FCSTD DOCUMENT  (FreeCAD 0.20R26155 (Git))
Label: snescart
License: All rights reserved
LicenseURL: http://en.wikipedia.org/wiki/All_rights_reserved
objects: Sketcher::SketchObject×5, PartDesign::Body×1
note: 6 computed .brp shape members not serialized (recipe doc carries the construction recipe); baked Part::Feature solids carry a one-line shape summary decoded from their .brp

FEATURE [Sketcher::SketchObject] Sketch  label="Edge_Cuts_0.15"
  FullyConstrained = true
  MapMode = 5
  Support = -> [XY_Plane]
  sketch-geometry (17):
    g0: LineSegment StartX=102 StartY=0 StartZ=0 EndX=102 EndY=17.5 EndZ=0
    g1: LineSegment StartX=102 StartY=17.5 StartZ=0 EndX=100.5 EndY=17.5 EndZ=0
    g2: LineSegment StartX=100.5 StartY=17.5 StartZ=0 EndX=100.5 EndY=23.5 EndZ=0
    g3: LineSegment StartX=100.5 StartY=23.5 StartZ=0 EndX=98 EndY=23.5 EndZ=0
    g4: LineSegment StartX=98 StartY=23.5 StartZ=0 EndX=98 EndY=25 EndZ=0
    g5: LineSegment StartX=98 StartY=25 StartZ=0 EndX=102 EndY=25 EndZ=0
    g6: LineSegment StartX=102 StartY=25 StartZ=0 EndX=102 EndY=48 EndZ=0
    g7: LineSegment StartX=98 StartY=52 StartZ=0 EndX=4 EndY=52 EndZ=0
    g8: LineSegment StartX=4e-14 StartY=48 StartZ=0 EndX=4e-14 EndY=16.4 EndZ=0
    g9: LineSegment StartX=4e-14 StartY=16.4 StartZ=0 EndX=4 EndY=16.4 EndZ=0
    g10: LineSegment StartX=4 StartY=16.4 StartZ=0 EndX=4 EndY=14.9 EndZ=0
    g11: LineSegment StartX=4 StartY=14.9 StartZ=0 EndX=1.5 EndY=14.9 EndZ=0
    g12: LineSegment StartX=1.5 StartY=14.9 StartZ=0 EndX=1.5 EndY=8.9 EndZ=0
    g13: LineSegment StartX=1.5 StartY=8.9 StartZ=0 EndX=0 EndY=8.9 EndZ=0
    g14: LineSegment StartX=0 StartY=8.9 StartZ=0 EndX=0 EndY=0 EndZ=0
    g15: ArcOfCircle CenterX=4 CenterY=48 CenterZ=0 NormalX=0 NormalY=0 NormalZ=1 AngleXU=0 Radius=4 StartAngle=1.5708 EndAngle=3.14159
    g16: ArcOfCircle CenterX=98 CenterY=48 CenterZ=0 NormalX=0 NormalY=0 NormalZ=1 AngleXU=0 Radius=4 StartAngle=1.84e-14 EndAngle=1.5708
  constraints (49):
    c: Vertical(g0)
    c: Coincident(g0,g1)
    c: Horizontal(g1)
    c: Coincident(g1,g2)
    c: Vertical(g2)
    c: Coincident(g2,g3)
    c: Horizontal(g3)
    c: Coincident(g3,g4)
    c: Vertical(g4)
    c: Coincident(g4,g5)
    c: Horizontal(g5)
    c: Coincident(g5,g6)
    c: Horizontal(g7)
    c: Vertical(g8)
    c: Coincident(g8,g9)
    c: Coincident(g9,g10)
    c: Vertical(g10)
    c: Coincident(g10,g11)
    c: Horizontal(g11)
    c: Coincident(g11,g12)
    c: Vertical(g12)
    c: Coincident(g12,g13)
    c: Horizontal(g13)
    c: Coincident(g13,g14)
    c: Vertical(g14)
    c: Horizontal(g9)
    c: Vertical(g6)
    c: DistanceX(g5,g5) = 4
    c: DistanceX(g2,g5) = 1.5
    c: DistanceX(g9,g9) = 4
    c: DistanceX(g11,g11) = 2.5
    c: DistanceX(g13,g13) = 1.5
    c: DistanceY(g10,g10) = 1.5
    c: DistanceY(g12,g12) = 6
    c: DistanceY(g14,g14) = 8.9
    c: DistanceY(g0,g5) = 25
    c: DistanceY(g4,g4) = 1.5
    c: DistanceY(g2,g2) = 6
    c: Coincident(g14,g-1)
    c: PointOnObject(g0,g-1)
    c: DistanceX(g14,g0) = 102
    c: Tangent(g7,g15) = -1.5708
    c: Tangent(g8,g15) = -1.5708
    c: Tangent(g6,g16) = -1.5708
    c: Tangent(g7,g16) = -1.5708
    c: Equal(g15,g16)
    c: DistanceX(g8,g6) = 102
    c: DistanceY(g14,g8) = 48
    c: Radius(g15) = 4
FEATURE [Sketcher::SketchObject] Sketch001  label="Edge_Cuts_0.016"
  FullyConstrained = true
  MapMode = 5
  Support = -> [XY_Plane]
  sketch-geometry (5):
    g0: LineSegment StartX=0 StartY=0 StartZ=0 EndX=21 EndY=0 EndZ=0
    g1: LineSegment StartX=21 StartY=0 StartZ=0 EndX=21 EndY=-10 EndZ=0
    g2: LineSegment StartX=21 StartY=-10 StartZ=0 EndX=81 EndY=-10 EndZ=0
    g3: LineSegment StartX=81 StartY=-10 StartZ=0 EndX=81 EndY=0 EndZ=0
    g4: LineSegment StartX=81 StartY=0 StartZ=0 EndX=102 EndY=0 EndZ=0
  constraints (15):
    c: Coincident(g-1,g0)
    c: PointOnObject(g0,g-1)
    c: Coincident(g0,g1)
    c: Vertical(g1)
    c: Coincident(g1,g2)
    c: Horizontal(g2)
    c: Coincident(g2,g3)
    c: PointOnObject(g3,g-1)
    c: Vertical(g3)
    c: Coincident(g3,g4)
    c: PointOnObject(g4,g-1)
    c: DistanceX(g0,g4) = 102
    c: Equal(g0,g4)
    c: DistanceX(g0,g0) = 21
    c: DistanceY(g3,g3) = 10
FEATURE [Sketcher::SketchObject] Sketch002  label="F_Pads_TH_SMD"
  ExternalGeometry = -> [Sketch001]
  FullyConstrained = true
  MapMode = 5
  Support = -> [XY_Plane]
  sketch-geometry (92):
    g0: LineSegment StartX=22.25 StartY=-3 StartZ=0 EndX=24.25 EndY=-3 EndZ=0
    g1: LineSegment StartX=24.25 StartY=-3 StartZ=0 EndX=24.25 EndY=-10 EndZ=0
    g2: LineSegment StartX=24.25 StartY=-10 StartZ=0 EndX=22.25 EndY=-10 EndZ=0
    g3: LineSegment StartX=22.25 StartY=-10 StartZ=0 EndX=22.25 EndY=-3 EndZ=0
    g4: LineSegment StartX=25.25 StartY=-3 StartZ=0 EndX=26.75 EndY=-3 EndZ=0
    g5: LineSegment StartX=26.75 StartY=-3 StartZ=0 EndX=26.75 EndY=-10 EndZ=0
    g6: LineSegment StartX=26.75 StartY=-10 StartZ=0 EndX=25.25 EndY=-10 EndZ=0
    g7: LineSegment StartX=25.25 StartY=-10 StartZ=0 EndX=25.25 EndY=-3 EndZ=0
    g8: LineSegment StartX=27.75 StartY=-3 StartZ=0 EndX=29.25 EndY=-3 EndZ=0
    g9: LineSegment StartX=29.25 StartY=-3 StartZ=0 EndX=29.25 EndY=-10 EndZ=0
    g10: LineSegment StartX=29.25 StartY=-10 StartZ=0 EndX=27.75 EndY=-10 EndZ=0
    g11: LineSegment StartX=27.75 StartY=-10 StartZ=0 EndX=27.75 EndY=-3 EndZ=0
    g12: LineSegment StartX=30.25 StartY=-10 StartZ=0 EndX=31.75 EndY=-10 EndZ=0
    g13: LineSegment StartX=31.75 StartY=-10 StartZ=0 EndX=31.75 EndY=-3 EndZ=0
    g14: LineSegment StartX=31.75 StartY=-3 StartZ=0 EndX=30.25 EndY=-3 EndZ=0
    g15: LineSegment StartX=30.25 StartY=-3 StartZ=0 EndX=30.25 EndY=-10 EndZ=0
    g16: LineSegment StartX=32.75 StartY=-10 StartZ=0 EndX=34.25 EndY=-10 EndZ=0
    g17: LineSegment StartX=34.25 StartY=-10 StartZ=0 EndX=34.25 EndY=-3 EndZ=0
    g18: LineSegment StartX=34.25 StartY=-3 StartZ=0 EndX=32.75 EndY=-3 EndZ=0
    g19: LineSegment StartX=32.75 StartY=-3 StartZ=0 EndX=32.75 EndY=-10 EndZ=0
    g20: LineSegment StartX=35.25 StartY=-10 StartZ=0 EndX=36.75 EndY=-10 EndZ=0
    g21: LineSegment StartX=36.75 StartY=-10 StartZ=0 EndX=36.75 EndY=-3 EndZ=0
    g22: LineSegment StartX=36.75 StartY=-3 StartZ=0 EndX=35.25 EndY=-3 EndZ=0
    g23: LineSegment StartX=35.25 StartY=-3 StartZ=0 EndX=35.25 EndY=-10 EndZ=0
    g24: LineSegment StartX=37.75 StartY=-10 StartZ=0 EndX=39.25 EndY=-10 EndZ=0
    g25: LineSegment StartX=39.25 StartY=-10 StartZ=0 EndX=39.25 EndY=-3 EndZ=0
    g26: LineSegment StartX=39.25 StartY=-3 StartZ=0 EndX=37.75 EndY=-3 EndZ=0
    g27: LineSegment StartX=37.75 StartY=-3 StartZ=0 EndX=37.75 EndY=-10 EndZ=0
    g28: LineSegment StartX=40.25 StartY=-10 StartZ=0 EndX=41.75 EndY=-10 EndZ=0
    g29: LineSegment StartX=41.75 StartY=-10 StartZ=0 EndX=41.75 EndY=-3 EndZ=0
    g30: LineSegment StartX=41.75 StartY=-3 StartZ=0 EndX=40.25 EndY=-3 EndZ=0
    g31: LineSegment StartX=40.25 StartY=-3 StartZ=0 EndX=40.25 EndY=-10 EndZ=0
    g32: LineSegment StartX=42.75 StartY=-10 StartZ=0 EndX=44.25 EndY=-10 EndZ=0
    g33: LineSegment StartX=44.25 StartY=-10 StartZ=0 EndX=44.25 EndY=-3 EndZ=0
    g34: LineSegment StartX=44.25 StartY=-3 StartZ=0 EndX=42.75 EndY=-3 EndZ=0
    g35: LineSegment StartX=42.75 StartY=-3 StartZ=0 EndX=42.75 EndY=-10 EndZ=0
    g36: LineSegment StartX=45.25 StartY=-10 StartZ=0 EndX=46.75 EndY=-10 EndZ=0
    g37: LineSegment StartX=46.75 StartY=-10 StartZ=0 EndX=46.75 EndY=-3 EndZ=0
    g38: LineSegment StartX=46.75 StartY=-3 StartZ=0 EndX=45.25 EndY=-3 EndZ=0
    g39: LineSegment StartX=45.25 StartY=-3 StartZ=0 EndX=45.25 EndY=-10 EndZ=0
    g40: LineSegment StartX=47.75 StartY=-10 StartZ=0 EndX=49.25 EndY=-10 EndZ=0
    g41: LineSegment StartX=49.25 StartY=-10 StartZ=0 EndX=49.25 EndY=-3 EndZ=0
    g42: LineSegment StartX=49.25 StartY=-3 StartZ=0 EndX=47.75 EndY=-3 EndZ=0
    g43: LineSegment StartX=47.75 StartY=-3 StartZ=0 EndX=47.75 EndY=-10 EndZ=0
    g44: LineSegment StartX=50.25 StartY=-10 StartZ=0 EndX=51.75 EndY=-10 EndZ=0
    g45: LineSegment StartX=51.75 StartY=-10 StartZ=0 EndX=51.75 EndY=-3 EndZ=0
    g46: LineSegment StartX=51.75 StartY=-3 StartZ=0 EndX=50.25 EndY=-3 EndZ=0
    g47: LineSegment StartX=50.25 StartY=-3 StartZ=0 EndX=50.25 EndY=-10 EndZ=0
    g48: LineSegment StartX=52.75 StartY=-10 StartZ=0 EndX=54.25 EndY=-10 EndZ=0
    g49: LineSegment StartX=54.25 StartY=-10 StartZ=0 EndX=54.25 EndY=-3 EndZ=0
    g50: LineSegment StartX=54.25 StartY=-3 StartZ=0 EndX=52.75 EndY=-3 EndZ=0
    g51: LineSegment StartX=52.75 StartY=-3 StartZ=0 EndX=52.75 EndY=-10 EndZ=0
    g52: LineSegment StartX=55.25 StartY=-10 StartZ=0 EndX=56.75 EndY=-10 EndZ=0
    g53: LineSegment StartX=56.75 StartY=-10 StartZ=0 EndX=56.75 EndY=-3 EndZ=0
    g54: LineSegment StartX=56.75 StartY=-3 StartZ=0 EndX=55.25 EndY=-3 EndZ=0
    g55: LineSegment StartX=55.25 StartY=-3 StartZ=0 EndX=55.25 EndY=-10 EndZ=0
    g56: LineSegment StartX=57.75 StartY=-10 StartZ=0 EndX=59.25 EndY=-10 EndZ=0
    g57: LineSegment StartX=59.25 StartY=-10 StartZ=0 EndX=59.25 EndY=-3 EndZ=0
    g58: LineSegment StartX=59.25 StartY=-3 StartZ=0 EndX=57.75 EndY=-3 EndZ=0
    g59: LineSegment StartX=57.75 StartY=-3 StartZ=0 EndX=57.75 EndY=-10 EndZ=0
    g60: LineSegment StartX=60.25 StartY=-10 StartZ=0 EndX=61.75 EndY=-10 EndZ=0
    g61: LineSegment StartX=61.75 StartY=-10 StartZ=0 EndX=61.75 EndY=-3 EndZ=0
    g62: LineSegment StartX=61.75 StartY=-3 StartZ=0 EndX=60.25 EndY=-3 EndZ=0
    g63: LineSegment StartX=60.25 StartY=-3 StartZ=0 EndX=60.25 EndY=-10 EndZ=0
    g64: LineSegment StartX=62.75 StartY=-10 StartZ=0 EndX=64.25 EndY=-10 EndZ=0
    g65: LineSegment StartX=64.25 StartY=-10 StartZ=0 EndX=64.25 EndY=-3 EndZ=0
    g66: LineSegment StartX=64.25 StartY=-3 StartZ=0 EndX=62.75 EndY=-3 EndZ=0
    g67: LineSegment StartX=62.75 StartY=-3 StartZ=0 EndX=62.75 EndY=-10 EndZ=0
    g68: LineSegment StartX=65.25 StartY=-10 StartZ=0 EndX=66.75 EndY=-10 EndZ=0
    g69: LineSegment StartX=66.75 StartY=-10 StartZ=0 EndX=66.75 EndY=-3 EndZ=0
    g70: LineSegment StartX=66.75 StartY=-3 StartZ=0 EndX=65.25 EndY=-3 EndZ=0
    g71: LineSegment StartX=65.25 StartY=-3 StartZ=0 EndX=65.25 EndY=-10 EndZ=0
    g72: LineSegment StartX=67.75 StartY=-10 StartZ=0 EndX=69.25 EndY=-10 EndZ=0
    g73: LineSegment StartX=69.25 StartY=-10 StartZ=0 EndX=69.25 EndY=-3 EndZ=0
    g74: LineSegment StartX=69.25 StartY=-3 StartZ=0 EndX=67.75 EndY=-3 EndZ=0
    g75: LineSegment StartX=67.75 StartY=-3 StartZ=0 EndX=67.75 EndY=-10 EndZ=0
    g76: LineSegment StartX=70.25 StartY=-10 StartZ=0 EndX=71.75 EndY=-10 EndZ=0
    g77: LineSegment StartX=71.75 StartY=-10 StartZ=0 EndX=71.75 EndY=-3 EndZ=0
    g78: LineSegment StartX=71.75 StartY=-3 StartZ=0 EndX=70.25 EndY=-3 EndZ=0
    g79: LineSegment StartX=70.25 StartY=-3 StartZ=0 EndX=70.25 EndY=-10 EndZ=0
    g80: LineSegment StartX=72.75 StartY=-10 StartZ=0 EndX=74.25 EndY=-10 EndZ=0
    g81: LineSegment StartX=74.25 StartY=-10 StartZ=0 EndX=74.25 EndY=-3 EndZ=0
    g82: LineSegment StartX=74.25 StartY=-3 StartZ=0 EndX=72.75 EndY=-3 EndZ=0
    g83: LineSegment StartX=72.75 StartY=-3 StartZ=0 EndX=72.75 EndY=-10 EndZ=0
    g84: LineSegment StartX=75.25 StartY=-10 StartZ=0 EndX=76.75 EndY=-10 EndZ=0
    g85: LineSegment StartX=76.75 StartY=-10 StartZ=0 EndX=76.75 EndY=-3 EndZ=0
    g86: LineSegment StartX=76.75 StartY=-3 StartZ=0 EndX=75.25 EndY=-3 EndZ=0
    g87: LineSegment StartX=75.25 StartY=-3 StartZ=0 EndX=75.25 EndY=-10 EndZ=0
    g88: LineSegment StartX=77.75 StartY=-10 StartZ=0 EndX=79.75 EndY=-10 EndZ=0
    g89: LineSegment StartX=79.75 StartY=-10 StartZ=0 EndX=79.75 EndY=-3 EndZ=0
    g90: LineSegment StartX=79.75 StartY=-3 StartZ=0 EndX=77.75 EndY=-3 EndZ=0
    g91: LineSegment StartX=77.75 StartY=-3 StartZ=0 EndX=77.75 EndY=-10 EndZ=0
  constraints (276):
    c: Coincident(g0,g1)
    c: Coincident(g1,g2)
    c: Coincident(g2,g3)
    c: Coincident(g3,g0)
    c: Horizontal(g0)
    c: Horizontal(g2)
    c: Vertical(g1)
    c: Vertical(g3)
    c: Coincident(g4,g5)
    c: Coincident(g5,g6)
    c: Coincident(g6,g7)
    c: Coincident(g7,g4)
    c: Horizontal(g4)
    c: Horizontal(g6)
    c: Vertical(g5)
    c: Vertical(g7)
    c: DistanceY(g3,g3) = 7
    c: PointOnObject(g1,g-4)
    c: PointOnObject(g6,g-4)
    c: DistanceX(g2,g2) = 2
    c: DistanceX(g6,g6) = 1.5
    c: Equal(g3,g7)
    c: DistanceX(g-4,g2) = 1.25
    c: DistanceX(g0,g4) = 1
    c: Coincident(g8,g9)
    c: Coincident(g9,g10)
    c: Coincident(g10,g11)
    c: Coincident(g11,g8)
    c: Horizontal(g8)
    c: Horizontal(g10)
    c: Vertical(g9)
    c: Vertical(g11)
    c: PointOnObject(g9,g-4)
    c: Coincident(g12,g13)
    c: Coincident(g13,g14)
    c: Coincident(g14,g15)
    c: Coincident(g15,g12)
    c: Horizontal(g12)
    c: Horizontal(g14)
    c: Vertical(g13)
    c: Vertical(g15)
    c: PointOnObject(g12,g-4)
    c: Coincident(g16,g17)
    c: Coincident(g17,g18)
    c: Coincident(g18,g19)
    c: Coincident(g19,g16)
    c: Horizontal(g16)
    c: Horizontal(g18)
    c: Vertical(g17)
    c: Vertical(g19)
    c: PointOnObject(g16,g-4)
    c: Coincident(g20,g21)
    c: Coincident(g21,g22)
    c: Coincident(g22,g23)
    c: Coincident(g23,g20)
    c: Horizontal(g20)
    c: Horizontal(g22)
    c: Vertical(g21)
    c: Vertical(g23)
    c: PointOnObject(g20,g-4)
    c: Coincident(g24,g25)
    c: Coincident(g25,g26)
    c: Coincident(g26,g27)
    c: Coincident(g27,g24)
    c: Horizontal(g24)
    c: Horizontal(g26)
    c: Vertical(g25)
    c: Vertical(g27)
    c: PointOnObject(g24,g-4)
    c: Coincident(g28,g29)
    c: Coincident(g29,g30)
    c: Coincident(g30,g31)
    c: Coincident(g31,g28)
    c: Horizontal(g28)
    c: Horizontal(g30)
    c: Vertical(g29)
    c: Vertical(g31)
    c: PointOnObject(g28,g-4)
    c: Coincident(g32,g33)
    c: Coincident(g33,g34)
    c: Coincident(g34,g35)
    c: Coincident(g35,g32)
    c: Horizontal(g32)
    c: Horizontal(g34)
    c: Vertical(g33)
    c: Vertical(g35)
    c: PointOnObject(g32,g-4)
    c: Coincident(g36,g37)
    c: Coincident(g37,g38)
    c: Coincident(g38,g39)
    c: Coincident(g39,g36)
    c: Horizontal(g36)
    c: Horizontal(g38)
    c: Vertical(g37)
    c: Vertical(g39)
    c: PointOnObject(g36,g-4)
    c: Coincident(g40,g41)
    c: Coincident(g41,g42)
    c: Coincident(g42,g43)
    c: Coincident(g43,g40)
    c: Horizontal(g40)
    c: Horizontal(g42)
    c: Vertical(g41)
    c: Vertical(g43)
    c: PointOnObject(g40,g-4)
    c: Coincident(g44,g45)
    c: Coincident(g45,g46)
    c: Coincident(g46,g47)
    c: Coincident(g47,g44)
    c: Horizontal(g44)
    c: Horizontal(g46)
    c: Vertical(g45)
    c: Vertical(g47)
    c: PointOnObject(g44,g-4)
    c: Coincident(g48,g49)
    c: Coincident(g49,g50)
    c: Coincident(g50,g51)
    c: Coincident(g51,g48)
    c: Horizontal(g48)
    c: Horizontal(g50)
    c: Vertical(g49)
    c: Vertical(g51)
    c: PointOnObject(g48,g-4)
    c: Coincident(g52,g53)
    c: Coincident(g53,g54)
    c: Coincident(g54,g55)
    c: Coincident(g55,g52)
    c: Horizontal(g52)
    c: Horizontal(g54)
    c: Vertical(g53)
    c: Vertical(g55)
    c: PointOnObject(g52,g-4)
    c: Coincident(g56,g57)
    c: Coincident(g57,g58)
    c: Coincident(g58,g59)
    c: Coincident(g59,g56)
    c: Horizontal(g56)
    c: Horizontal(g58)
    c: Vertical(g57)
    c: Vertical(g59)
    c: PointOnObject(g56,g-4)
    c: Coincident(g60,g61)
    c: Coincident(g61,g62)
    c: Coincident(g62,g63)
    c: Coincident(g63,g60)
    c: Horizontal(g60)
    c: Horizontal(g62)
    c: Vertical(g61)
    c: Vertical(g63)
    c: PointOnObject(g60,g-4)
    c: Coincident(g64,g65)
    c: Coincident(g65,g66)
    c: Coincident(g66,g67)
    c: Coincident(g67,g64)
    c: Horizontal(g64)
    c: Horizontal(g66)
    c: Vertical(g65)
    c: Vertical(g67)
    c: PointOnObject(g64,g-4)
    c: Coincident(g68,g69)
    c: Coincident(g69,g70)
    c: Coincident(g70,g71)
    c: Coincident(g71,g68)
    c: Horizontal(g68)
    c: Horizontal(g70)
    c: Vertical(g69)
    c: Vertical(g71)
    c: PointOnObject(g68,g-4)
    c: Coincident(g72,g73)
    c: Coincident(g73,g74)
    c: Coincident(g74,g75)
    c: Coincident(g75,g72)
    c: Horizontal(g72)
    c: Horizontal(g74)
    c: Vertical(g73)
    c: Vertical(g75)
    c: PointOnObject(g72,g-4)
    c: Coincident(g76,g77)
    c: Coincident(g77,g78)
    c: Coincident(g78,g79)
    c: Coincident(g79,g76)
    c: Horizontal(g76)
    c: Horizontal(g78)
    c: Vertical(g77)
    c: Vertical(g79)
    c: PointOnObject(g76,g-4)
    c: Equal(g11,g15)
    c: Equal(g15,g19)
    c: Equal(g19,g23)
    c: Equal(g23,g27)
    c: Equal(g27,g31)
    c: Equal(g31,g35)
    c: Equal(g35,g39)
    c: Equal(g39,g43)
    c: Equal(g43,g47)
    c: Equal(g47,g51)
    c: Equal(g51,g55)
    c: Equal(g55,g59)
    c: Equal(g59,g63)
    c: Equal(g63,g67)
    c: Equal(g67,g71)
    c: Equal(g71,g75)
    c: Equal(g75,g79)
    c: Equal(g79,g7)
    c: Equal(g54,g58)
    c: Equal(g58,g62)
    c: Equal(g62,g66)
    c: Equal(g66,g70)
    c: Equal(g70,g74)
    c: Equal(g74,g78)
    c: Equal(g78,g50)
    c: Equal(g50,g46)
    c: Equal(g46,g42)
    c: Equal(g42,g38)
    c: Equal(g38,g34)
    c: Equal(g34,g30)
    c: Equal(g30,g26)
    c: Equal(g26,g22)
    c: Equal(g22,g18)
    c: Equal(g18,g14)
    c: Equal(g14,g8)
    c: Equal(g8,g4)
    c: DistanceX(g5,g10) = 1
    c: DistanceX(g9,g12) = 1
    c: DistanceX(g12,g16) = 1
    c: DistanceX(g16,g20) = 1
    c: DistanceX(g20,g24) = 1
    c: DistanceX(g24,g28) = 1
    c: DistanceX(g28,g32) = 1
    c: DistanceX(g32,g36) = 1
    c: DistanceX(g36,g40) = 1
    c: DistanceX(g40,g44) = 1
    c: DistanceX(g44,g48) = 1
    c: DistanceX(g48,g52) = 1
    c: DistanceX(g52,g56) = 1
    c: DistanceX(g56,g60) = 1
    c: DistanceX(g60,g64) = 1
    c: DistanceX(g64,g68) = 1
    c: DistanceX(g68,g72) = 1
    c: DistanceX(g72,g76) = 1
    c: Coincident(g80,g81)
    c: Coincident(g81,g82)
    c: Coincident(g82,g83)
    c: Coincident(g83,g80)
    c: Horizontal(g80)
    c: Horizontal(g82)
    c: Vertical(g81)
    c: Vertical(g83)
    c: PointOnObject(g80,g-4)
    c: Coincident(g84,g85)
    c: Coincident(g85,g86)
    c: Coincident(g86,g87)
    c: Coincident(g87,g84)
    c: Horizontal(g84)
    c: Horizontal(g86)
    c: Vertical(g85)
    c: Vertical(g87)
    c: PointOnObject(g84,g-4)
    c: Coincident(g88,g89)
    c: Coincident(g89,g90)
    c: Coincident(g90,g91)
    c: Coincident(g91,g88)
    c: Horizontal(g88)
    c: Horizontal(g90)
    c: Vertical(g89)
    c: Vertical(g91)
    c: PointOnObject(g88,g-4)
    c: Equal(g83,g87)
    c: Equal(g87,g91)
    c: Equal(g86,g82)
    c: Equal(g82,g78)
    c: DistanceX(g76,g80) = 1
    c: DistanceX(g80,g84) = 1
    c: DistanceX(g84,g88) = 1
    c: DistanceX(g90,g90) = 2
    c: Equal(g83,g77)
FEATURE [Sketcher::SketchObject] Sketch003  label="B_Pads_TH_SMD"
  ExternalGeometry = -> [Sketch001]
  FullyConstrained = true
  MapMode = 5
  Support = -> [XY_Plane]
  sketch-geometry (92):
    g0: LineSegment StartX=22.25 StartY=-3 StartZ=0 EndX=24.25 EndY=-3 EndZ=0
    g1: LineSegment StartX=24.25 StartY=-3 StartZ=0 EndX=24.25 EndY=-10 EndZ=0
    g2: LineSegment StartX=24.25 StartY=-10 StartZ=0 EndX=22.25 EndY=-10 EndZ=0
    g3: LineSegment StartX=22.25 StartY=-10 StartZ=0 EndX=22.25 EndY=-3 EndZ=0
    g4: LineSegment StartX=25.25 StartY=-3 StartZ=0 EndX=26.75 EndY=-3 EndZ=0
    g5: LineSegment StartX=26.75 StartY=-3 StartZ=0 EndX=26.75 EndY=-10 EndZ=0
    g6: LineSegment StartX=26.75 StartY=-10 StartZ=0 EndX=25.25 EndY=-10 EndZ=0
    g7: LineSegment StartX=25.25 StartY=-10 StartZ=0 EndX=25.25 EndY=-3 EndZ=0
    g8: LineSegment StartX=27.75 StartY=-3 StartZ=0 EndX=29.25 EndY=-3 EndZ=0
    g9: LineSegment StartX=29.25 StartY=-3 StartZ=0 EndX=29.25 EndY=-10 EndZ=0
    g10: LineSegment StartX=29.25 StartY=-10 StartZ=0 EndX=27.75 EndY=-10 EndZ=0
    g11: LineSegment StartX=27.75 StartY=-10 StartZ=0 EndX=27.75 EndY=-3 EndZ=0
    g12: LineSegment StartX=30.25 StartY=-10 StartZ=0 EndX=31.75 EndY=-10 EndZ=0
    g13: LineSegment StartX=31.75 StartY=-10 StartZ=0 EndX=31.75 EndY=-3 EndZ=0
    g14: LineSegment StartX=31.75 StartY=-3 StartZ=0 EndX=30.25 EndY=-3 EndZ=0
    g15: LineSegment StartX=30.25 StartY=-3 StartZ=0 EndX=30.25 EndY=-10 EndZ=0
    g16: LineSegment StartX=32.75 StartY=-10 StartZ=0 EndX=34.25 EndY=-10 EndZ=0
    g17: LineSegment StartX=34.25 StartY=-10 StartZ=0 EndX=34.25 EndY=-3 EndZ=0
    g18: LineSegment StartX=34.25 StartY=-3 StartZ=0 EndX=32.75 EndY=-3 EndZ=0
    g19: LineSegment StartX=32.75 StartY=-3 StartZ=0 EndX=32.75 EndY=-10 EndZ=0
    g20: LineSegment StartX=35.25 StartY=-10 StartZ=0 EndX=36.75 EndY=-10 EndZ=0
    g21: LineSegment StartX=36.75 StartY=-10 StartZ=0 EndX=36.75 EndY=-3 EndZ=0
    g22: LineSegment StartX=36.75 StartY=-3 StartZ=0 EndX=35.25 EndY=-3 EndZ=0
    g23: LineSegment StartX=35.25 StartY=-3 StartZ=0 EndX=35.25 EndY=-10 EndZ=0
    g24: LineSegment StartX=37.75 StartY=-10 StartZ=0 EndX=39.25 EndY=-10 EndZ=0
    g25: LineSegment StartX=39.25 StartY=-10 StartZ=0 EndX=39.25 EndY=-3 EndZ=0
    g26: LineSegment StartX=39.25 StartY=-3 StartZ=0 EndX=37.75 EndY=-3 EndZ=0
    g27: LineSegment StartX=37.75 StartY=-3 StartZ=0 EndX=37.75 EndY=-10 EndZ=0
    g28: LineSegment StartX=40.25 StartY=-10 StartZ=0 EndX=41.75 EndY=-10 EndZ=0
    g29: LineSegment StartX=41.75 StartY=-10 StartZ=0 EndX=41.75 EndY=-3 EndZ=0
    g30: LineSegment StartX=41.75 StartY=-3 StartZ=0 EndX=40.25 EndY=-3 EndZ=0
    g31: LineSegment StartX=40.25 StartY=-3 StartZ=0 EndX=40.25 EndY=-10 EndZ=0
    g32: LineSegment StartX=42.75 StartY=-10 StartZ=0 EndX=44.25 EndY=-10 EndZ=0
    g33: LineSegment StartX=44.25 StartY=-10 StartZ=0 EndX=44.25 EndY=-3 EndZ=0
    g34: LineSegment StartX=44.25 StartY=-3 StartZ=0 EndX=42.75 EndY=-3 EndZ=0
    g35: LineSegment StartX=42.75 StartY=-3 StartZ=0 EndX=42.75 EndY=-10 EndZ=0
    g36: LineSegment StartX=45.25 StartY=-10 StartZ=0 EndX=46.75 EndY=-10 EndZ=0
    g37: LineSegment StartX=46.75 StartY=-10 StartZ=0 EndX=46.75 EndY=-3 EndZ=0
    g38: LineSegment StartX=46.75 StartY=-3 StartZ=0 EndX=45.25 EndY=-3 EndZ=0
    g39: LineSegment StartX=45.25 StartY=-3 StartZ=0 EndX=45.25 EndY=-10 EndZ=0
    g40: LineSegment StartX=47.75 StartY=-10 StartZ=0 EndX=49.25 EndY=-10 EndZ=0
    g41: LineSegment StartX=49.25 StartY=-10 StartZ=0 EndX=49.25 EndY=-3 EndZ=0
    g42: LineSegment StartX=49.25 StartY=-3 StartZ=0 EndX=47.75 EndY=-3 EndZ=0
    g43: LineSegment StartX=47.75 StartY=-3 StartZ=0 EndX=47.75 EndY=-10 EndZ=0
    g44: LineSegment StartX=50.25 StartY=-10 StartZ=0 EndX=51.75 EndY=-10 EndZ=0
    g45: LineSegment StartX=51.75 StartY=-10 StartZ=0 EndX=51.75 EndY=-3 EndZ=0
    g46: LineSegment StartX=51.75 StartY=-3 StartZ=0 EndX=50.25 EndY=-3 EndZ=0
    g47: LineSegment StartX=50.25 StartY=-3 StartZ=0 EndX=50.25 EndY=-10 EndZ=0
    g48: LineSegment StartX=52.75 StartY=-10 StartZ=0 EndX=54.25 EndY=-10 EndZ=0
    g49: LineSegment StartX=54.25 StartY=-10 StartZ=0 EndX=54.25 EndY=-3 EndZ=0
    g50: LineSegment StartX=54.25 StartY=-3 StartZ=0 EndX=52.75 EndY=-3 EndZ=0
    g51: LineSegment StartX=52.75 StartY=-3 StartZ=0 EndX=52.75 EndY=-10 EndZ=0
    g52: LineSegment StartX=55.25 StartY=-10 StartZ=0 EndX=56.75 EndY=-10 EndZ=0
    g53: LineSegment StartX=56.75 StartY=-10 StartZ=0 EndX=56.75 EndY=-3 EndZ=0
    g54: LineSegment StartX=56.75 StartY=-3 StartZ=0 EndX=55.25 EndY=-3 EndZ=0
    g55: LineSegment StartX=55.25 StartY=-3 StartZ=0 EndX=55.25 EndY=-10 EndZ=0
    g56: LineSegment StartX=57.75 StartY=-10 StartZ=0 EndX=59.25 EndY=-10 EndZ=0
    g57: LineSegment StartX=59.25 StartY=-10 StartZ=0 EndX=59.25 EndY=-3 EndZ=0
    g58: LineSegment StartX=59.25 StartY=-3 StartZ=0 EndX=57.75 EndY=-3 EndZ=0
    g59: LineSegment StartX=57.75 StartY=-3 StartZ=0 EndX=57.75 EndY=-10 EndZ=0
    g60: LineSegment StartX=60.25 StartY=-10 StartZ=0 EndX=61.75 EndY=-10 EndZ=0
    g61: LineSegment StartX=61.75 StartY=-10 StartZ=0 EndX=61.75 EndY=-3 EndZ=0
    g62: LineSegment StartX=61.75 StartY=-3 StartZ=0 EndX=60.25 EndY=-3 EndZ=0
    g63: LineSegment StartX=60.25 StartY=-3 StartZ=0 EndX=60.25 EndY=-10 EndZ=0
    g64: LineSegment StartX=62.75 StartY=-10 StartZ=0 EndX=64.25 EndY=-10 EndZ=0
    g65: LineSegment StartX=64.25 StartY=-10 StartZ=0 EndX=64.25 EndY=-3 EndZ=0
    g66: LineSegment StartX=64.25 StartY=-3 StartZ=0 EndX=62.75 EndY=-3 EndZ=0
    g67: LineSegment StartX=62.75 StartY=-3 StartZ=0 EndX=62.75 EndY=-10 EndZ=0
    g68: LineSegment StartX=65.25 StartY=-10 StartZ=0 EndX=66.75 EndY=-10 EndZ=0
    g69: LineSegment StartX=66.75 StartY=-10 StartZ=0 EndX=66.75 EndY=-3 EndZ=0
    g70: LineSegment StartX=66.75 StartY=-3 StartZ=0 EndX=65.25 EndY=-3 EndZ=0
    g71: LineSegment StartX=65.25 StartY=-3 StartZ=0 EndX=65.25 EndY=-10 EndZ=0
    g72: LineSegment StartX=67.75 StartY=-10 StartZ=0 EndX=69.25 EndY=-10 EndZ=0
    g73: LineSegment StartX=69.25 StartY=-10 StartZ=0 EndX=69.25 EndY=-3 EndZ=0
    g74: LineSegment StartX=69.25 StartY=-3 StartZ=0 EndX=67.75 EndY=-3 EndZ=0
    g75: LineSegment StartX=67.75 StartY=-3 StartZ=0 EndX=67.75 EndY=-10 EndZ=0
    g76: LineSegment StartX=70.25 StartY=-10 StartZ=0 EndX=71.75 EndY=-10 EndZ=0
    g77: LineSegment StartX=71.75 StartY=-10 StartZ=0 EndX=71.75 EndY=-3 EndZ=0
    g78: LineSegment StartX=71.75 StartY=-3 StartZ=0 EndX=70.25 EndY=-3 EndZ=0
    g79: LineSegment StartX=70.25 StartY=-3 StartZ=0 EndX=70.25 EndY=-10 EndZ=0
    g80: LineSegment StartX=72.75 StartY=-10 StartZ=0 EndX=74.25 EndY=-10 EndZ=0
    g81: LineSegment StartX=74.25 StartY=-10 StartZ=0 EndX=74.25 EndY=-3 EndZ=0
    g82: LineSegment StartX=74.25 StartY=-3 StartZ=0 EndX=72.75 EndY=-3 EndZ=0
    g83: LineSegment StartX=72.75 StartY=-3 StartZ=0 EndX=72.75 EndY=-10 EndZ=0
    g84: LineSegment StartX=75.25 StartY=-10 StartZ=0 EndX=76.75 EndY=-10 EndZ=0
    g85: LineSegment StartX=76.75 StartY=-10 StartZ=0 EndX=76.75 EndY=-3 EndZ=0
    g86: LineSegment StartX=76.75 StartY=-3 StartZ=0 EndX=75.25 EndY=-3 EndZ=0
    g87: LineSegment StartX=75.25 StartY=-3 StartZ=0 EndX=75.25 EndY=-10 EndZ=0
    g88: LineSegment StartX=77.75 StartY=-10 StartZ=0 EndX=79.75 EndY=-10 EndZ=0
    g89: LineSegment StartX=79.75 StartY=-10 StartZ=0 EndX=79.75 EndY=-3 EndZ=0
    g90: LineSegment StartX=79.75 StartY=-3 StartZ=0 EndX=77.75 EndY=-3 EndZ=0
    g91: LineSegment StartX=77.75 StartY=-3 StartZ=0 EndX=77.75 EndY=-10 EndZ=0
  constraints (276):
    c: Coincident(g0,g1)
    c: Coincident(g1,g2)
    c: Coincident(g2,g3)
    c: Coincident(g3,g0)
    c: Horizontal(g0)
    c: Horizontal(g2)
    c: Vertical(g1)
    c: Vertical(g3)
    c: Coincident(g4,g5)
    c: Coincident(g5,g6)
    c: Coincident(g6,g7)
    c: Coincident(g7,g4)
    c: Horizontal(g4)
    c: Horizontal(g6)
    c: Vertical(g5)
    c: Vertical(g7)
    c: DistanceY(g3,g3) = 7
    c: PointOnObject(g1,g-4)
    c: PointOnObject(g6,g-4)
    c: DistanceX(g2,g2) = 2
    c: DistanceX(g6,g6) = 1.5
    c: Equal(g3,g7)
    c: DistanceX(g-4,g2) = 1.25
    c: DistanceX(g0,g4) = 1
    c: Coincident(g8,g9)
    c: Coincident(g9,g10)
    c: Coincident(g10,g11)
    c: Coincident(g11,g8)
    c: Horizontal(g8)
    c: Horizontal(g10)
    c: Vertical(g9)
    c: Vertical(g11)
    c: PointOnObject(g9,g-4)
    c: Coincident(g12,g13)
    c: Coincident(g13,g14)
    c: Coincident(g14,g15)
    c: Coincident(g15,g12)
    c: Horizontal(g12)
    c: Horizontal(g14)
    c: Vertical(g13)
    c: Vertical(g15)
    c: PointOnObject(g12,g-4)
    c: Coincident(g16,g17)
    c: Coincident(g17,g18)
    c: Coincident(g18,g19)
    c: Coincident(g19,g16)
    c: Horizontal(g16)
    c: Horizontal(g18)
    c: Vertical(g17)
    c: Vertical(g19)
    c: PointOnObject(g16,g-4)
    c: Coincident(g20,g21)
    c: Coincident(g21,g22)
    c: Coincident(g22,g23)
    c: Coincident(g23,g20)
    c: Horizontal(g20)
    c: Horizontal(g22)
    c: Vertical(g21)
    c: Vertical(g23)
    c: PointOnObject(g20,g-4)
    c: Coincident(g24,g25)
    c: Coincident(g25,g26)
    c: Coincident(g26,g27)
    c: Coincident(g27,g24)
    c: Horizontal(g24)
    c: Horizontal(g26)
    c: Vertical(g25)
    c: Vertical(g27)
    c: PointOnObject(g24,g-4)
    c: Coincident(g28,g29)
    c: Coincident(g29,g30)
    c: Coincident(g30,g31)
    c: Coincident(g31,g28)
    c: Horizontal(g28)
    c: Horizontal(g30)
    c: Vertical(g29)
    c: Vertical(g31)
    c: PointOnObject(g28,g-4)
    c: Coincident(g32,g33)
    c: Coincident(g33,g34)
    c: Coincident(g34,g35)
    c: Coincident(g35,g32)
    c: Horizontal(g32)
    c: Horizontal(g34)
    c: Vertical(g33)
    c: Vertical(g35)
    c: PointOnObject(g32,g-4)
    c: Coincident(g36,g37)
    c: Coincident(g37,g38)
    c: Coincident(g38,g39)
    c: Coincident(g39,g36)
    c: Horizontal(g36)
    c: Horizontal(g38)
    c: Vertical(g37)
    c: Vertical(g39)
    c: PointOnObject(g36,g-4)
    c: Coincident(g40,g41)
    c: Coincident(g41,g42)
    c: Coincident(g42,g43)
    c: Coincident(g43,g40)
    c: Horizontal(g40)
    c: Horizontal(g42)
    c: Vertical(g41)
    c: Vertical(g43)
    c: PointOnObject(g40,g-4)
    c: Coincident(g44,g45)
    c: Coincident(g45,g46)
    c: Coincident(g46,g47)
    c: Coincident(g47,g44)
    c: Horizontal(g44)
    c: Horizontal(g46)
    c: Vertical(g45)
    c: Vertical(g47)
    c: PointOnObject(g44,g-4)
    c: Coincident(g48,g49)
    c: Coincident(g49,g50)
    c: Coincident(g50,g51)
    c: Coincident(g51,g48)
    c: Horizontal(g48)
    c: Horizontal(g50)
    c: Vertical(g49)
    c: Vertical(g51)
    c: PointOnObject(g48,g-4)
    c: Coincident(g52,g53)
    c: Coincident(g53,g54)
    c: Coincident(g54,g55)
    c: Coincident(g55,g52)
    c: Horizontal(g52)
    c: Horizontal(g54)
    c: Vertical(g53)
    c: Vertical(g55)
    c: PointOnObject(g52,g-4)
    c: Coincident(g56,g57)
    c: Coincident(g57,g58)
    c: Coincident(g58,g59)
    c: Coincident(g59,g56)
    c: Horizontal(g56)
    c: Horizontal(g58)
    c: Vertical(g57)
    c: Vertical(g59)
    c: PointOnObject(g56,g-4)
    c: Coincident(g60,g61)
    c: Coincident(g61,g62)
    c: Coincident(g62,g63)
    c: Coincident(g63,g60)
    c: Horizontal(g60)
    c: Horizontal(g62)
    c: Vertical(g61)
    c: Vertical(g63)
    c: PointOnObject(g60,g-4)
    c: Coincident(g64,g65)
    c: Coincident(g65,g66)
    c: Coincident(g66,g67)
    c: Coincident(g67,g64)
    c: Horizontal(g64)
    c: Horizontal(g66)
    c: Vertical(g65)
    c: Vertical(g67)
    c: PointOnObject(g64,g-4)
    c: Coincident(g68,g69)
    c: Coincident(g69,g70)
    c: Coincident(g70,g71)
    c: Coincident(g71,g68)
    c: Horizontal(g68)
    c: Horizontal(g70)
    c: Vertical(g69)
    c: Vertical(g71)
    c: PointOnObject(g68,g-4)
    c: Coincident(g72,g73)
    c: Coincident(g73,g74)
    c: Coincident(g74,g75)
    c: Coincident(g75,g72)
    c: Horizontal(g72)
    c: Horizontal(g74)
    c: Vertical(g73)
    c: Vertical(g75)
    c: PointOnObject(g72,g-4)
    c: Coincident(g76,g77)
    c: Coincident(g77,g78)
    c: Coincident(g78,g79)
    c: Coincident(g79,g76)
    c: Horizontal(g76)
    c: Horizontal(g78)
    c: Vertical(g77)
    c: Vertical(g79)
    c: PointOnObject(g76,g-4)
    c: Equal(g11,g15)
    c: Equal(g15,g19)
    c: Equal(g19,g23)
    c: Equal(g23,g27)
    c: Equal(g27,g31)
    c: Equal(g31,g35)
    c: Equal(g35,g39)
    c: Equal(g39,g43)
    c: Equal(g43,g47)
    c: Equal(g47,g51)
    c: Equal(g51,g55)
    c: Equal(g55,g59)
    c: Equal(g59,g63)
    c: Equal(g63,g67)
    c: Equal(g67,g71)
    c: Equal(g71,g75)
    c: Equal(g75,g79)
    c: Equal(g79,g7)
    c: Equal(g54,g58)
    c: Equal(g58,g62)
    c: Equal(g62,g66)
    c: Equal(g66,g70)
    c: Equal(g70,g74)
    c: Equal(g74,g78)
    c: Equal(g78,g50)
    c: Equal(g50,g46)
    c: Equal(g46,g42)
    c: Equal(g42,g38)
    c: Equal(g38,g34)
    c: Equal(g34,g30)
    c: Equal(g30,g26)
    c: Equal(g26,g22)
    c: Equal(g22,g18)
    c: Equal(g18,g14)
    c: Equal(g14,g8)
    c: Equal(g8,g4)
    c: DistanceX(g5,g10) = 1
    c: DistanceX(g9,g12) = 1
    c: DistanceX(g12,g16) = 1
    c: DistanceX(g16,g20) = 1
    c: DistanceX(g20,g24) = 1
    c: DistanceX(g24,g28) = 1
    c: DistanceX(g28,g32) = 1
    c: DistanceX(g32,g36) = 1
    c: DistanceX(g36,g40) = 1
    c: DistanceX(g40,g44) = 1
    c: DistanceX(g44,g48) = 1
    c: DistanceX(g48,g52) = 1
    c: DistanceX(g52,g56) = 1
    c: DistanceX(g56,g60) = 1
    c: DistanceX(g60,g64) = 1
    c: DistanceX(g64,g68) = 1
    c: DistanceX(g68,g72) = 1
    c: DistanceX(g72,g76) = 1
    c: Coincident(g80,g81)
    c: Coincident(g81,g82)
    c: Coincident(g82,g83)
    c: Coincident(g83,g80)
    c: Horizontal(g80)
    c: Horizontal(g82)
    c: Vertical(g81)
    c: Vertical(g83)
    c: PointOnObject(g80,g-4)
    c: Coincident(g84,g85)
    c: Coincident(g85,g86)
    c: Coincident(g86,g87)
    c: Coincident(g87,g84)
    c: Horizontal(g84)
    c: Horizontal(g86)
    c: Vertical(g85)
    c: Vertical(g87)
    c: PointOnObject(g84,g-4)
    c: Coincident(g88,g89)
    c: Coincident(g89,g90)
    c: Coincident(g90,g91)
    c: Coincident(g91,g88)
    c: Horizontal(g88)
    c: Horizontal(g90)
    c: Vertical(g89)
    c: Vertical(g91)
    c: PointOnObject(g88,g-4)
    c: Equal(g83,g87)
    c: Equal(g87,g91)
    c: Equal(g86,g82)
    c: Equal(g82,g78)
    c: DistanceX(g76,g80) = 1
    c: DistanceX(g80,g84) = 1
    c: DistanceX(g84,g88) = 1
    c: DistanceX(g90,g90) = 2
    c: Equal(g83,g77)
FEATURE [Sketcher::SketchObject] Sketch004  label="F_Fab_0.1"
  FullyConstrained = true
  MapMode = 5
  Support = -> [XY_Plane]
  sketch-geometry (1):
    g0: Circle CenterX=48 CenterY=20 CenterZ=0 NormalX=0 NormalY=0 NormalZ=1 AngleXU=0 Radius=3
  constraints (3):
    c: Radius(g0) = 3
    c: DistanceX(g-1,g0) = 48
    c: DistanceY(g-1,g0) = 20
FEATURE [PartDesign::Body] Body
  Group = -> [Sketch,Sketch001,Sketch002,Sketch003,Sketch004]
  Origin = -> Origin
